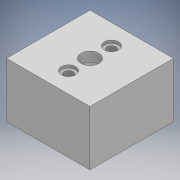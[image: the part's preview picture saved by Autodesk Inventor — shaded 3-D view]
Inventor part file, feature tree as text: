
AUTODESK INVENTOR PART (.ipt)
format: ipt  version: 2018.2 (Build 222227000, 227)  size: 127,488 bytes
history: native  units: mm
features: extrude x3, sketch x3
ambient origin geometry x8: Origin, YZ Plane, XZ Plane, XY Plane, X Axis, Y Axis, Z Axis, Center Point
bodies: Solid1 (feature_tree)
feature tree (6):
  extrude  "Extrusion1"  Depth=35.0mm
  extrude  "Extrusion2"  Depth=19.0mm TaperAngle=0.0deg
  extrude  "Extrusion3"  Depth=1.2mm
  sketch  "Sketch1"  dims[d0=35.0mm d1=35.0mm]
  sketch  "Sketch2"  dims[d2=25.5mm d3=19.0mm d4=0.0mm]
  sketch  "Sketch3"  dims[d5=7.5mm d6=17.5mm d7=17.5mm d8=3.7mm d9=3.7mm d10=9.0mm d11=9.0mm d12=4.0mm d13=0.0mm d14=6.0mm d15=6.0mm d16=1.2mm d17=0.0mm]
